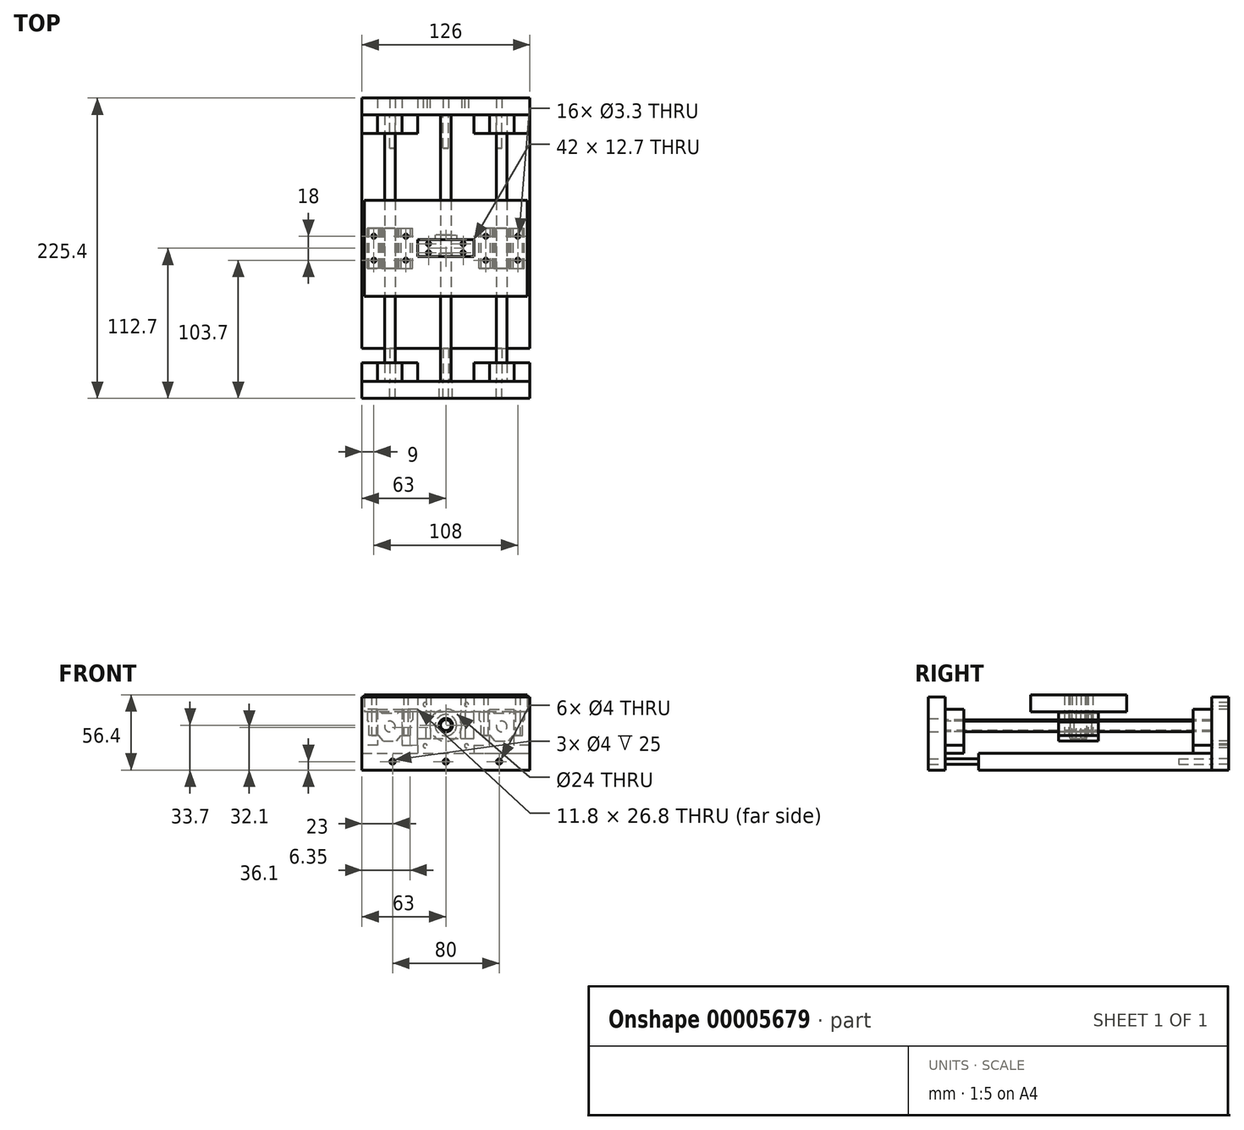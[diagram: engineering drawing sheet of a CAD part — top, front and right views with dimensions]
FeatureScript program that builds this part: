
annotation { "Feature Type Name" : "Feature", "Feature Type Description" : "" }
export const myFeature = defineFeature(function(context is Context, id is Id, definition is map)
    precondition{}
    {
        {
            var Q0;
            Q0=qCreatedBy(makeId("Top.planeOp"),FACE);
            var sketch = newSketch(context, id + "F0", { "sketchPlane" : qUnion([Q0])});
            skLineSegment(sketch, "E0.bottom", {"start": v(-63, 100) * mm, "end": v(63, 100) * mm});
            skLineSegment(sketch, "E0.top", {"start": v(-63, -100) * mm, "end": v(63, -100) * mm});
            skLineSegment(sketch, "E0.left", {"start": v(-63, 100) * mm, "end": v(-63, -100) * mm});
            skLineSegment(sketch, "E0.right", {"start": v(63, 100) * mm, "end": v(63, -100) * mm});
            skLineSegment(sketch, "E1", {"start": v(-63, 0) * mm, "end": v(63, 0) * mm, "construction": true});
            skSolve(sketch);
        }
        {
            var Q0;
            Q0=makeQuery(id+"F0.imprint","IMPRINT",FACE,{"disambiguationData":[TD([[makeQuery(id+"F0.imprint","IMPRINT",EDGE,{"derivedFrom":sQuery(id+"F0.wireOp",EDGE,"E0.bottom")}),-1.0]])]});
            extrude(context, id + "F1", {"entities" : qUnion([Q0]), "depth" : 12.7 * mm});
        }
        {
            var Q0;
            Q0=makeQuery(id+"F1.opExtrude","SWEPT_FACE",FACE,{"disambiguationData":[OSD([sQuery(id+"F0.wireOp",EDGE,"E0.bottom")])]});
            var sketch = newSketch(context, id + "F2", { "sketchPlane" : qUnion([Q0])});
            skPoint(sketch, "E2", {"position": v(0, 33.7) * mm});
            skCircle(sketch, "E3", {"center": v(0, 33.7) * mm, "radius": 12 * mm});
            skLineSegment(sketch, "E4.bottom", {"start": v(-63, 12.7) * mm, "end": v(63, 12.7) * mm, "construction": true});
            skLineSegment(sketch, "E4.top", {"start": v(-63, 54.7) * mm, "end": v(63, 54.7) * mm});
            skLineSegment(sketch, "E4.left", {"start": v(-63, 12.7) * mm, "end": v(-63, 54.7) * mm});
            skLineSegment(sketch, "E4.right", {"start": v(63, 12.7) * mm, "end": v(63, 54.7) * mm});
            skLineSegment(sketch, "E5", {"start": v(0, 54.7) * mm, "end": v(0, 12.7) * mm, "construction": true});
            skLineSegment(sketch, "E6", {"start": v(-63, 33.7) * mm, "end": v(63, 33.7) * mm, "construction": true});
            skLineSegment(sketch, "E7.rect.bottom", {"start": v(15.5, 49.2) * mm, "end": v(-15.5, 49.2) * mm, "construction": true});
            skLineSegment(sketch, "E7.rect.top", {"start": v(15.5, 18.2) * mm, "end": v(-15.5, 18.2) * mm, "construction": true});
            skLineSegment(sketch, "E7.rect.left", {"start": v(15.5, 49.2) * mm, "end": v(15.5, 18.2) * mm, "construction": true});
            skLineSegment(sketch, "E7.rect.right", {"start": v(-15.5, 49.2) * mm, "end": v(-15.5, 18.2) * mm, "construction": true});
            skCircle(sketch, "E8", {"center": v(-15.5, 49.2) * mm, "radius": 1.5 * mm});
            skCircle(sketch, "E9", {"center": v(15.5, 49.2) * mm, "radius": 1.5 * mm});
            skCircle(sketch, "E10", {"center": v(-15.5, 18.2) * mm, "radius": 1.5 * mm});
            skCircle(sketch, "E11", {"center": v(15.5, 18.2) * mm, "radius": 1.5 * mm});
            skLineSegment(sketch, "E12.rect.bottom", {"start": v(21, 12.7) * mm, "end": v(-21, 12.7) * mm, "construction": true});
            skLineSegment(sketch, "E12.rect.top", {"start": v(21, 54.7) * mm, "end": v(-21, 54.7) * mm, "construction": true});
            skLineSegment(sketch, "E12.rect.left", {"start": v(21, 12.7) * mm, "end": v(21, 54.7) * mm, "construction": true});
            skLineSegment(sketch, "E12.rect.right", {"start": v(-21, 12.7) * mm, "end": v(-21, 54.7) * mm, "construction": true});
            skLineSegment(sketch, "E13.0", {"start": v(-63, 12.7) * mm, "end": v(-63, 0) * mm});
            skLineSegment(sketch, "E14.0", {"start": v(63, 12.7) * mm, "end": v(63, 0) * mm});
            skLineSegment(sketch, "E15.0", {"start": v(63, 0) * mm, "end": v(-63, 0) * mm});
            skLineSegment(sketch, "E16.0.0", {"start": v(-63, 0) * mm, "end": v(63, 0) * mm});
            skLineSegment(sketch, "E16.0.1", {"start": v(63, 0) * mm, "end": v(63, 12.7) * mm});
            skLineSegment(sketch, "E16.0.2", {"start": v(63, 12.7) * mm, "end": v(-63, 12.7) * mm});
            skLineSegment(sketch, "E17", {"start": v(-63, 6.35) * mm, "end": v(63, 6.35) * mm, "construction": true});
            skLineSegment(sketch, "E18", {"start": v(0, 0) * mm, "end": v(0, 12.7) * mm, "construction": true});
            skPoint(sketch, "E19", {"position": v(0, 6.35) * mm});
            skCircle(sketch, "E20", {"center": v(0, 6.35) * mm, "radius": 2 * mm});
            skCircle(sketch, "E21.1.0.0", {"center": v(40, 6.35) * mm, "radius": 2 * mm});
            skLineSegment(sketch, "E21.direction1", {"start": v(0, 6.35) * mm, "end": v(40, 6.35) * mm, "construction": true});
            skCircle(sketch, "E22.1.0.0", {"center": v(-40, 6.35) * mm, "radius": 2 * mm});
            skLineSegment(sketch, "E22.direction1", {"start": v(0, 6.35) * mm, "end": v(-40, 6.35) * mm, "construction": true});
            skSolve(sketch);
        }
        {
            var Q0;
            Q0=makeQuery(id+"F2.imprint","IMPRINT",FACE,{"disambiguationData":[TD([[makeQuery(id+"F2.imprint","IMPRINT",EDGE,{"derivedFrom":sQuery(id+"F2.wireOp",EDGE,"E22.1.0.0")}),1.0]])]});
            var Q1;
            Q1=makeQuery(id+"F2.imprint","IMPRINT",FACE,{"disambiguationData":[TD([[makeQuery(id+"F2.imprint","IMPRINT",EDGE,{"derivedFrom":sQuery(id+"F2.wireOp",EDGE,"E20")}),1.0]])]});
            var Q2;
            Q2=makeQuery(id+"F2.imprint","IMPRINT",FACE,{"disambiguationData":[TD([[makeQuery(id+"F2.imprint","IMPRINT",EDGE,{"derivedFrom":sQuery(id+"F2.wireOp",EDGE,"E21.1.0.0")}),1.0]])]});
            extrude(context, id + "F3", {"entities" : qUnion([Q0, Q1, Q2]), "operationType" : NewBodyOperationType.REMOVE, "oppositeDirection" : true, "depth" : 25 * mm});
        }
        {
            var Q0;
            Q0 = qSketchRegion(id + "F2", true);
            extrude(context, id + "F4", {"entities" : qUnion([Q0]), "depth" : 12.7 * mm});
        }
        {
            var Q0;
            Q0=makeQuery(id+"F1.opExtrude","SWEPT_FACE",FACE,{"disambiguationData":[OSD([sQuery(id+"F0.wireOp",EDGE,"E0.top")])]});
            var sketch = newSketch(context, id + "F5", { "sketchPlane" : qUnion([Q0])});
            skLineSegment(sketch, "E23.0", {"start": v(63, 54.7) * mm, "end": v(-63, 54.7) * mm});
            skLineSegment(sketch, "E24.0", {"start": v(-63, 12.7) * mm, "end": v(63, 12.7) * mm, "construction": true});
            skLineSegment(sketch, "E25.0", {"start": v(-63, 0) * mm, "end": v(63, 0) * mm});
            skLineSegment(sketch, "E26.0", {"start": v(-63, 54.7) * mm, "end": v(-63, 0) * mm});
            skLineSegment(sketch, "E27.0", {"start": v(63, 54.7) * mm, "end": v(63, 0) * mm});
            skCircle(sketch, "E28.0", {"center": v(40, 6.35) * mm, "radius": 2 * mm});
            skCircle(sketch, "E29.0", {"center": v(0, 6.35) * mm, "radius": 2 * mm});
            skCircle(sketch, "E30.0", {"center": v(-40, 6.35) * mm, "radius": 2 * mm});
            skLineSegment(sketch, "E31", {"start": v(0, 54.7) * mm, "end": v(0, 12.7) * mm, "construction": true});
            skPoint(sketch, "E32", {"position": v(0, 33.7) * mm});
            skCircle(sketch, "E33", {"center": v(0, 33.7) * mm, "radius": 4 * mm});
            skSolve(sketch);
        }
        {
            var Q0;
            {var subQ2=sQuery(id+"F5.wireOp",EDGE,"E25.0");Q0=makeQuery(id+"F5.imprint","IMPRINT",FACE,{"disambiguationData":[TD([[makeQuery(id+"F5.imprint","IMPRINT",EDGE,{"derivedFrom":subQ2}),1.0]])]});}
            var Q1;
            {var subQ2=sQuery(id+"F5.wireOp",EDGE,"E23.0");Q1=makeQuery(id+"F5.imprint","IMPRINT",FACE,{"disambiguationData":[TD([[makeQuery(id+"F5.imprint","IMPRINT",EDGE,{"derivedFrom":subQ2}),1.0]])]});}
            extrude(context, id + "F6", {"entities" : qUnion([Q0, Q1]), "depth" : 12.7 * mm});
        }
        {
            var Q0;
            Q0=makeQuery(id+"F1.opExtrude","SWEPT_FACE",FACE,{"disambiguationData":[OSD([sQuery(id+"F0.wireOp",EDGE,"E0.top")])]});
            var sketch = newSketch(context, id + "F7", { "sketchPlane" : qUnion([Q0])});
            skCircle(sketch, "E34.0", {"center": v(-40, 6.35) * mm, "radius": 2 * mm});
            skCircle(sketch, "E35.0", {"center": v(0, 6.35) * mm, "radius": 2 * mm});
            skCircle(sketch, "E36.0", {"center": v(40, 6.35) * mm, "radius": 2 * mm});
            skSolve(sketch);
        }
        {
            var Q0;
            Q0=makeQuery(id+"F7.imprint","IMPRINT",FACE,{"disambiguationData":[TD([[makeQuery(id+"F7.imprint","IMPRINT",EDGE,{"derivedFrom":sQuery(id+"F7.wireOp",EDGE,"E34.0")}),-1.0]])]});
            var Q1;
            Q1=makeQuery(id+"F7.imprint","IMPRINT",FACE,{"disambiguationData":[TD([[makeQuery(id+"F7.imprint","IMPRINT",EDGE,{"derivedFrom":sQuery(id+"F7.wireOp",EDGE,"E35.0")}),-1.0]])]});
            var Q2;
            Q2=makeQuery(id+"F7.imprint","IMPRINT",FACE,{"disambiguationData":[TD([[makeQuery(id+"F7.imprint","IMPRINT",EDGE,{"derivedFrom":sQuery(id+"F7.wireOp",EDGE,"E36.0")}),-1.0]])]});
            extrude(context, id + "F8", {"entities" : qUnion([Q0, Q1, Q2]), "operationType" : NewBodyOperationType.REMOVE, "oppositeDirection" : true, "depth" : 25 * mm});
        }
        {
            var Q0;
            Q0=makeQuery(id+"F1.opExtrude","CAP_FACE",FACE,{"disambiguationData":[OSD([sQuery(id+"F0.wireOp",EDGE,"E0.bottom"),sQuery(id+"F0.wireOp",EDGE,"E0.top"),sQuery(id+"F0.wireOp",EDGE,"E0.left"),sQuery(id+"F0.wireOp",EDGE,"E0.right")])],"isStart":false});
            var sketch = newSketch(context, id + "F9", { "sketchPlane" : qUnion([Q0])});
            skLineSegment(sketch, "E37.bottom", {"start": v(-63, 100) * mm, "end": v(-21, 100) * mm});
            skLineSegment(sketch, "E37.top", {"start": v(-63, 86) * mm, "end": v(-21, 86) * mm});
            skLineSegment(sketch, "E37.left", {"start": v(-63, 100) * mm, "end": v(-63, 86) * mm});
            skLineSegment(sketch, "E37.right", {"start": v(-21, 100) * mm, "end": v(-21, 86) * mm});
            skSolve(sketch);
        }
        {
            var Q0;
            Q0=makeQuery(id+"F9.imprint","IMPRINT",FACE,{"disambiguationData":[TD([[makeQuery(id+"F9.imprint","IMPRINT",EDGE,{"derivedFrom":sQuery(id+"F9.wireOp",EDGE,"E37.bottom")}),-1.0]])]});
            extrude(context, id + "F10", {"entities" : qUnion([Q0]), "depth" : 32.8 * mm});
        }
        {
            var Q0;
            Q0=makeQuery(id+"F10.opExtrude","SWEPT_FACE",FACE,{"disambiguationData":[OSD([sQuery(id+"F9.wireOp",EDGE,"E37.top")])]});
            var sketch = newSketch(context, id + "F11", { "sketchPlane" : qUnion([Q0])});
            skLineSegment(sketch, "E38", {"start": v(-21, 18.7) * mm, "end": v(-32.8, 18.7) * mm});
            skLineSegment(sketch, "E39", {"start": v(-32.8, 18.7) * mm, "end": v(-32.8, 45.5) * mm});
            skLineSegment(sketch, "E40", {"start": v(-42, 45.5) * mm, "end": v(-42, 12.7) * mm, "construction": true});
            skLineSegment(sketch, "E41.0.MirrorCS", {"start": v(-51.2, 18.7) * mm, "end": v(-51.2, 45.5) * mm});
            skLineSegment(sketch, "E42.0.MirrorCS", {"start": v(-63, 18.7) * mm, "end": v(-51.2, 18.7) * mm});
            skSolve(sketch);
        }
        {
            var Q0;
            {var subQ5=sQuery(id+"F11.wireOp",EDGE,"E38");Q0=makeQuery(id+"F11.imprint","IMPRINT",FACE,{"disambiguationData":[TD([[makeQuery(id+"F11.imprint","IMPRINT",EDGE,{"derivedFrom":subQ5}),-1.0]])]});}
            var Q1;
            {var subQ2=sQuery(id+"F11.wireOp",EDGE,"E41.0.MirrorCS");Q1=makeQuery(id+"F11.imprint","IMPRINT",FACE,{"disambiguationData":[TD([[makeQuery(id+"F11.imprint","IMPRINT",EDGE,{"derivedFrom":subQ2}),1.0]])]});}
            extrude(context, id + "F12", {"entities" : qUnion([Q0, Q1]), "operationType" : NewBodyOperationType.REMOVE, "endBound" : BoundingType.THROUGH_ALL, "oppositeDirection" : true, "depth" : 25 * mm});
        }
        {
            var Q0;
            Q0=makeQuery(id+"F10.opExtrude","SWEPT_BODY",BODY,{"disambiguationData":[OSD([sQuery(id+"F9.wireOp",EDGE,"E37.bottom"),sQuery(id+"F9.wireOp",EDGE,"E37.top"),sQuery(id+"F9.wireOp",EDGE,"E37.left"),sQuery(id+"F9.wireOp",EDGE,"E37.right")])]});
            transform(context, id + "F13", {"entities" : qUnion([Q0]), "transformType" : TransformType.TRANSLATION_3D, "dx" : 0 * mm, "dy" : -186 * mm, "dz" : 0 * mm, "makeCopy" : true});
        }
        {
            var Q0;
            Q0=makeQuery(id+"F10.opExtrude","SWEPT_BODY",BODY,{"disambiguationData":[OSD([sQuery(id+"F9.wireOp",EDGE,"E37.bottom"),sQuery(id+"F9.wireOp",EDGE,"E37.top"),sQuery(id+"F9.wireOp",EDGE,"E37.left"),sQuery(id+"F9.wireOp",EDGE,"E37.right")])]});
            var Q1;
            Q1=makeQuery(id+"F13.opPattern","COPY",BODY,{"derivedFrom":makeQuery(id+"F10.opExtrude","SWEPT_BODY",BODY,{"disambiguationData":[OSD([sQuery(id+"F9.wireOp",EDGE,"E37.bottom"),sQuery(id+"F9.wireOp",EDGE,"E37.top"),sQuery(id+"F9.wireOp",EDGE,"E37.left"),sQuery(id+"F9.wireOp",EDGE,"E37.right")])]}),"instanceName":"1"});
            transform(context, id + "F14", {"entities" : qUnion([Q0, Q1]), "transformType" : TransformType.TRANSLATION_3D, "dx" : 84 * mm, "dy" : 0 * mm, "dz" : 0 * mm, "makeCopy" : true});
        }
        {
            var Q0;
            Q0=makeQuery(id+"F13.opPattern","COPY",FACE,{"derivedFrom":makeQuery(id+"F10.opExtrude","SWEPT_FACE",FACE,{"disambiguationData":[OSD([sQuery(id+"F9.wireOp",EDGE,"E37.top")])]}),"instanceName":"1"});
            var sketch = newSketch(context, id + "F15", { "sketchPlane" : qUnion([Q0])});
            skLineSegment(sketch, "E43", {"start": v(-42, 45.5) * mm, "end": v(-42, 12.7) * mm, "construction": true});
            skCircle(sketch, "E44", {"center": v(-42, 32.7) * mm, "radius": 4 * mm});
            skSolve(sketch);
        }
        {
            var Q0;
            Q0=makeQuery(id+"F15.imprint","IMPRINT",FACE,{"disambiguationData":[TD([[makeQuery(id+"F15.imprint","IMPRINT",EDGE,{"derivedFrom":sQuery(id+"F15.wireOp",EDGE,"E44")}),1.0]])]});
            var Q1;
            Q1=sQuery(id+"F15.wireOp",EDGE,"E44");
            extrude(context, id + "F16", {"entities" : qUnion([Q0]), "surfaceEntities" : qUnion([Q1]), "oppositeDirection" : true, "depth" : 200 * mm});
        }
        {
            var Q0;
            Q0=makeQuery(id+"F13.opPattern","COPY",BODY,{"derivedFrom":makeQuery(id+"F10.opExtrude","SWEPT_BODY",BODY,{"disambiguationData":[OSD([sQuery(id+"F9.wireOp",EDGE,"E37.bottom"),sQuery(id+"F9.wireOp",EDGE,"E37.top"),sQuery(id+"F9.wireOp",EDGE,"E37.left"),sQuery(id+"F9.wireOp",EDGE,"E37.right")])]}),"instanceName":"1"});
            transform(context, id + "F17", {"entities" : qUnion([Q0]), "transformType" : TransformType.TRANSLATION_3D, "dx" : 84 * mm, "dy" : 0 * mm, "dz" : 0 * mm, "makeCopy" : true});
        }
        {
            var Q0;
            Q0=makeQuery(id+"F17.opPattern","COPY",BODY,{"derivedFrom":makeQuery(id+"F13.opPattern","COPY",BODY,{"derivedFrom":makeQuery(id+"F10.opExtrude","SWEPT_BODY",BODY,{"disambiguationData":[OSD([sQuery(id+"F9.wireOp",EDGE,"E37.bottom"),sQuery(id+"F9.wireOp",EDGE,"E37.top"),sQuery(id+"F9.wireOp",EDGE,"E37.left"),sQuery(id+"F9.wireOp",EDGE,"E37.right")])]}),"instanceName":"1"}),"instanceName":"1"});
            deleteBodies(context, id + "F18", {"entities" : qUnion([Q0])});
        }
        {
            var Q0;
            Q0=makeQuery(id+"F16.opExtrude","SWEPT_BODY",BODY,{"disambiguationData":[OSD([sQuery(id+"F15.wireOp",EDGE,"E44")])]});
            transform(context, id + "F19", {"entities" : qUnion([Q0]), "transformType" : TransformType.TRANSLATION_3D, "dx" : 84 * mm, "dy" : 0 * mm, "dz" : 0 * mm, "makeCopy" : true});
        }
        {
            var Q0;
            Q0=qCreatedBy(makeId("Front.planeOp"),FACE);
            var sketch = newSketch(context, id + "F20", { "sketchPlane" : qUnion([Q0])});
            skLineSegment(sketch, "E45.rect.bottom", {"start": v(-25, 21.7) * mm, "end": v(-35, 21.7) * mm});
            skLineSegment(sketch, "E45.rect.top", {"start": v(-37, 43.7) * mm, "end": v(-47, 43.7) * mm});
            skLineSegment(sketch, "E45.rect.left", {"start": v(-25, 21.7) * mm, "end": v(-25, 27.7) * mm});
            skLineSegment(sketch, "E45.rect.right", {"start": v(-59, 21.7) * mm, "end": v(-59, 27.7) * mm});
            skPoint(sketch, "E45.rect.middle", {"position": v(-42, 32.7) * mm});
            skCircle(sketch, "E46", {"center": v(-42, 32.7) * mm, "radius": 4 * mm});
            skLineSegment(sketch, "E47", {"start": v(-42, 43.7) * mm, "end": v(-42, 21.7) * mm, "construction": true});
            skLineSegment(sketch, "E48", {"start": v(-37, 43.7) * mm, "end": v(-33.5, 39.4) * mm});
            skLineSegment(sketch, "E49", {"start": v(-33.5, 39.4) * mm, "end": v(-26.5, 39.4) * mm});
            skCircle(sketch, "E50", {"center": v(-42, 32.7) * mm, "radius": 7.5 * mm});
            skLineSegment(sketch, "E51.0.MirrorCS", {"start": v(-47, 43.7) * mm, "end": v(-50.5, 39.4) * mm});
            skLineSegment(sketch, "E52.0.MirrorCS", {"start": v(-50.5, 39.4) * mm, "end": v(-57.5, 39.4) * mm});
            skLineSegment(sketch, "E53", {"start": v(-42, 22.7) * mm, "end": v(-36, 22.7) * mm});
            skLineSegment(sketch, "E54", {"start": v(-36, 22.7) * mm, "end": v(-35, 21.7) * mm});
            skLineSegment(sketch, "E55.0.MirrorCS", {"start": v(-42, 22.7) * mm, "end": v(-48, 22.7) * mm});
            skLineSegment(sketch, "E56.0.MirrorCS", {"start": v(-48, 22.7) * mm, "end": v(-49, 21.7) * mm});
            skLineSegment(sketch, "E57.trimOffspring", {"start": v(-49, 21.7) * mm, "end": v(-59, 21.7) * mm});
            skLineSegment(sketch, "E58", {"start": v(-26.5, 39.4) * mm, "end": v(-26.5, 29.4) * mm});
            skLineSegment(sketch, "E59", {"start": v(-26.5, 29.4) * mm, "end": v(-25, 27.7) * mm});
            skLineSegment(sketch, "E60.0.MirrorCS", {"start": v(-57.5, 39.4) * mm, "end": v(-57.5, 29.4) * mm});
            skLineSegment(sketch, "E61.0.MirrorCS", {"start": v(-57.5, 29.4) * mm, "end": v(-59, 27.7) * mm});
            skSolve(sketch);
        }
        {
            var Q0;
            Q0=makeQuery(id+"F20.imprint","IMPRINT",FACE,{"disambiguationData":[TD([[makeQuery(id+"F20.imprint","IMPRINT",EDGE,{"derivedFrom":sQuery(id+"F20.wireOp",EDGE,"E45.rect.bottom")}),-1.0]])]});
            var Q1;
            Q1=makeQuery(id+"F20.imprint","IMPRINT",FACE,{"disambiguationData":[TD([[makeQuery(id+"F20.imprint","IMPRINT",EDGE,{"derivedFrom":sQuery(id+"F20.wireOp",EDGE,"E46")}),-1.0]])]});
            extrude(context, id + "F21", {"entities" : qUnion([Q0, Q1]), "depth" : 30 * mm, "symmetric" : true});
        }
        {
            var Q0;
            Q0=makeQuery(id+"F21.opExtrude","SWEPT_BODY",BODY,{"disambiguationData":[OSD([sQuery(id+"F20.wireOp",EDGE,"E45.rect.bottom"),sQuery(id+"F20.wireOp",EDGE,"E45.rect.top"),sQuery(id+"F20.wireOp",EDGE,"E45.rect.left"),sQuery(id+"F20.wireOp",EDGE,"E45.rect.right"),sQuery(id+"F20.wireOp",EDGE,"E46"),sQuery(id+"F20.wireOp",EDGE,"E48"),sQuery(id+"F20.wireOp",EDGE,"E49"),sQuery(id+"F20.wireOp",EDGE,"E51.0.MirrorCS"),sQuery(id+"F20.wireOp",EDGE,"E52.0.MirrorCS"),sQuery(id+"F20.wireOp",EDGE,"E53"),sQuery(id+"F20.wireOp",EDGE,"E54"),sQuery(id+"F20.wireOp",EDGE,"E55.0.MirrorCS"),sQuery(id+"F20.wireOp",EDGE,"E56.0.MirrorCS"),sQuery(id+"F20.wireOp",EDGE,"E57.trimOffspring"),sQuery(id+"F20.wireOp",EDGE,"E58"),sQuery(id+"F20.wireOp",EDGE,"E59"),sQuery(id+"F20.wireOp",EDGE,"E60.0.MirrorCS"),sQuery(id+"F20.wireOp",EDGE,"E61.0.MirrorCS")])]});
            var Q1;
            Q1=makeQuery(id+"F21.opExtrude","SWEPT_FACE",FACE,{"disambiguationData":[OSD([sQuery(id+"F20.wireOp",EDGE,"E46")])]});
            transform(context, id + "F22", {"entities" : qUnion([Q0]), "transformType" : TransformType.ROTATION, "transformAxis" : qUnion([Q1]), "angle" : 180 * degree, "makeCopy" : false});
        }
        {
            var Q0;
            Q0=makeQuery(id+"F21.opExtrude","SWEPT_FACE",FACE,{"disambiguationData":[OSD([sQuery(id+"F20.wireOp",EDGE,"E45.rect.top")])]});
            var sketch = newSketch(context, id + "F23", { "sketchPlane" : qUnion([Q0])});
            skCircle(sketch, "E62", {"center": v(-30, 9) * mm, "radius": 1.65 * mm});
            skLineSegment(sketch, "E63", {"start": v(-42, 15) * mm, "end": v(-42, -15) * mm, "construction": true});
            skCircle(sketch, "E64.0.MirrorC", {"center": v(-54, 9) * mm, "radius": 1.65 * mm});
            skLineSegment(sketch, "E65", {"start": v(-59, 0) * mm, "end": v(-25, 0) * mm, "construction": true});
            skCircle(sketch, "E66.0.MirrorC", {"center": v(-30, -9) * mm, "radius": 1.65 * mm});
            skCircle(sketch, "E67.0.MirrorC", {"center": v(-54, -9) * mm, "radius": 1.65 * mm});
            skSolve(sketch);
        }
        {
            var Q0;
            Q0=makeQuery(id+"F23.imprint","IMPRINT",FACE,{"disambiguationData":[TD([[makeQuery(id+"F23.imprint","IMPRINT",EDGE,{"derivedFrom":sQuery(id+"F23.wireOp",EDGE,"E66.0.MirrorC")}),-1.0]])]});
            var Q1;
            Q1=makeQuery(id+"F23.imprint","IMPRINT",FACE,{"disambiguationData":[TD([[makeQuery(id+"F23.imprint","IMPRINT",EDGE,{"derivedFrom":sQuery(id+"F23.wireOp",EDGE,"E62")}),1.0]])]});
            var Q2;
            Q2=makeQuery(id+"F23.imprint","IMPRINT",FACE,{"disambiguationData":[TD([[makeQuery(id+"F23.imprint","IMPRINT",EDGE,{"derivedFrom":sQuery(id+"F23.wireOp",EDGE,"E64.0.MirrorC")}),-1.0]])]});
            var Q3;
            Q3=makeQuery(id+"F23.imprint","IMPRINT",FACE,{"disambiguationData":[TD([[makeQuery(id+"F23.imprint","IMPRINT",EDGE,{"derivedFrom":sQuery(id+"F23.wireOp",EDGE,"E67.0.MirrorC")}),1.0]])]});
            extrude(context, id + "F24", {"entities" : qUnion([Q0, Q1, Q2, Q3]), "operationType" : NewBodyOperationType.REMOVE, "endBound" : BoundingType.THROUGH_ALL, "oppositeDirection" : true, "depth" : 25 * mm});
        }
        {
            var Q0;
            Q0=makeQuery(id+"F21.opExtrude","SWEPT_BODY",BODY,{"disambiguationData":[OSD([sQuery(id+"F20.wireOp",EDGE,"E45.rect.bottom"),sQuery(id+"F20.wireOp",EDGE,"E45.rect.top"),sQuery(id+"F20.wireOp",EDGE,"E45.rect.left"),sQuery(id+"F20.wireOp",EDGE,"E45.rect.right"),sQuery(id+"F20.wireOp",EDGE,"E46"),sQuery(id+"F20.wireOp",EDGE,"E48"),sQuery(id+"F20.wireOp",EDGE,"E49"),sQuery(id+"F20.wireOp",EDGE,"E51.0.MirrorCS"),sQuery(id+"F20.wireOp",EDGE,"E52.0.MirrorCS"),sQuery(id+"F20.wireOp",EDGE,"E53"),sQuery(id+"F20.wireOp",EDGE,"E54"),sQuery(id+"F20.wireOp",EDGE,"E55.0.MirrorCS"),sQuery(id+"F20.wireOp",EDGE,"E56.0.MirrorCS"),sQuery(id+"F20.wireOp",EDGE,"E57.trimOffspring"),sQuery(id+"F20.wireOp",EDGE,"E58"),sQuery(id+"F20.wireOp",EDGE,"E59"),sQuery(id+"F20.wireOp",EDGE,"E60.0.MirrorCS"),sQuery(id+"F20.wireOp",EDGE,"E61.0.MirrorCS")])]});
            transform(context, id + "F25", {"entities" : qUnion([Q0]), "transformType" : TransformType.TRANSLATION_3D, "dx" : 84 * mm, "dy" : 0 * mm, "dz" : 0 * mm, "makeCopy" : true});
        }
        {
            var Q0;
            Q0=makeQuery(id+"F21.opExtrude","SWEPT_FACE",FACE,{"disambiguationData":[OSD([sQuery(id+"F20.wireOp",EDGE,"E45.rect.bottom")])]});
            var sketch = newSketch(context, id + "F26", { "sketchPlane" : qUnion([Q0])});
            skLineSegment(sketch, "E68.0", {"start": v(-63, 100) * mm, "end": v(-63, -100) * mm});
            skLineSegment(sketch, "E69.0", {"start": v(63, 100) * mm, "end": v(63, -100) * mm});
            skCircle(sketch, "E70.0", {"center": v(-54, 9) * mm, "radius": 1.65 * mm});
            skCircle(sketch, "E71.0", {"center": v(-54, -9) * mm, "radius": 1.65 * mm});
            skCircle(sketch, "E72.0", {"center": v(-30, -9) * mm, "radius": 1.65 * mm});
            skCircle(sketch, "E73.0", {"center": v(-30, 9) * mm, "radius": 1.65 * mm});
            skCircle(sketch, "E74.0", {"center": v(30, 9) * mm, "radius": 1.65 * mm});
            skCircle(sketch, "E75.0", {"center": v(30, -9) * mm, "radius": 1.65 * mm});
            skCircle(sketch, "E76.0", {"center": v(54, 9) * mm, "radius": 1.65 * mm});
            skCircle(sketch, "E77.0", {"center": v(54, -9) * mm, "radius": 1.65 * mm});
            skLineSegment(sketch, "E78", {"start": v(-63, 0) * mm, "end": v(63, 0) * mm, "construction": true});
            skLineSegment(sketch, "E79.rect.bottom", {"start": v(61, 36) * mm, "end": v(-61, 36) * mm});
            skLineSegment(sketch, "E79.rect.top", {"start": v(61, -36) * mm, "end": v(-61, -36) * mm});
            skLineSegment(sketch, "E79.rect.left", {"start": v(61, 36) * mm, "end": v(61, -36) * mm});
            skLineSegment(sketch, "E79.rect.right", {"start": v(-61, 36) * mm, "end": v(-61, -36) * mm});
            skPoint(sketch, "E79.rect.middle", {"position": v(0, 0) * mm});
            skSolve(sketch);
        }
        {
            var Q0;
            Q0 = qSketchRegion(id + "F26", true);
            extrude(context, id + "F27", {"entities" : qUnion([Q0]), "depth" : 12.7 * mm});
        }
        {
            var Q0;
            Q0=makeQuery(id+"F27.opExtrude","CAP_FACE",FACE,{"disambiguationData":[OSD([sQuery(id+"F26.wireOp",EDGE,"E70.0"),sQuery(id+"F26.wireOp",EDGE,"E71.0"),sQuery(id+"F26.wireOp",EDGE,"E72.0"),sQuery(id+"F26.wireOp",EDGE,"E73.0"),sQuery(id+"F26.wireOp",EDGE,"E74.0"),sQuery(id+"F26.wireOp",EDGE,"E75.0"),sQuery(id+"F26.wireOp",EDGE,"E76.0"),sQuery(id+"F26.wireOp",EDGE,"E77.0"),sQuery(id+"F26.wireOp",EDGE,"E79.rect.bottom"),sQuery(id+"F26.wireOp",EDGE,"E79.rect.top"),sQuery(id+"F26.wireOp",EDGE,"E79.rect.left"),sQuery(id+"F26.wireOp",EDGE,"E79.rect.right")])],"isStart":true});
            var sketch = newSketch(context, id + "F28", { "sketchPlane" : qUnion([Q0])});
            skLineSegment(sketch, "E80", {"start": v(0, -36) * mm, "end": v(0, 36) * mm, "construction": true});
            skLineSegment(sketch, "E81.rect.bottom", {"start": v(-21, 6.35) * mm, "end": v(21, 6.35) * mm});
            skLineSegment(sketch, "E81.rect.top", {"start": v(-21, -6.35) * mm, "end": v(21, -6.35) * mm});
            skLineSegment(sketch, "E81.rect.left", {"start": v(-21, 6.35) * mm, "end": v(-21, -6.35) * mm});
            skLineSegment(sketch, "E81.rect.right", {"start": v(21, 6.35) * mm, "end": v(21, -6.35) * mm});
            skPoint(sketch, "E81.rect.middle", {"position": v(0, 0) * mm});
            skLineSegment(sketch, "E82", {"start": v(21, 0) * mm, "end": v(-21, 0) * mm, "construction": true});
            skCircle(sketch, "E83", {"center": v(13, -3.35) * mm, "radius": 1.65 * mm});
            skCircle(sketch, "E84.0.MirrorC", {"center": v(-13, -3.35) * mm, "radius": 1.65 * mm});
            skCircle(sketch, "E85.0.MirrorC", {"center": v(13, 3.35) * mm, "radius": 1.65 * mm});
            skCircle(sketch, "E86.0.MirrorC", {"center": v(-13, 3.35) * mm, "radius": 1.65 * mm});
            skSolve(sketch);
        }
        {
            var Q0;
            Q0=makeQuery(id+"F28.imprint","IMPRINT",FACE,{"disambiguationData":[TD([[makeQuery(id+"F28.imprint","IMPRINT",EDGE,{"derivedFrom":sQuery(id+"F28.wireOp",EDGE,"E81.rect.bottom")}),-1.0]])]});
            extrude(context, id + "F29", {"entities" : qUnion([Q0]), "depth" : 20 * mm});
        }
        {
            var Q0;
            Q0=makeQuery(id+"F29.opExtrude","SWEPT_FACE",FACE,{"disambiguationData":[OSD([sQuery(id+"F28.wireOp",EDGE,"E81.rect.top")])]});
            var sketch = newSketch(context, id + "F30", { "sketchPlane" : qUnion([Q0])});
            skPoint(sketch, "E87.0", {"position": v(0, 33.7) * mm});
            skCircle(sketch, "E88", {"center": v(0, 33.7) * mm, "radius": 5 * mm});
            skSolve(sketch);
        }
        {
            var Q0;
            Q0=makeQuery(id+"F30.imprint","IMPRINT",FACE,{"disambiguationData":[TD([[makeQuery(id+"F30.imprint","IMPRINT",EDGE,{"derivedFrom":sQuery(id+"F30.wireOp",EDGE,"E88")}),1.0]])]});
            extrude(context, id + "F31", {"entities" : qUnion([Q0]), "operationType" : NewBodyOperationType.REMOVE, "endBound" : BoundingType.THROUGH_ALL, "oppositeDirection" : true, "depth" : 25 * mm});
        }
        {
            var Q0;
            Q0=makeQuery(id+"F29.opExtrude","SWEPT_FACE",FACE,{"disambiguationData":[OSD([sQuery(id+"F28.wireOp",EDGE,"E81.rect.top")])]});
            var sketch = newSketch(context, id + "F32", { "sketchPlane" : qUnion([Q0])});
            skPoint(sketch, "E89.0", {"position": v(0, 33.7) * mm});
            skCircle(sketch, "E90", {"center": v(0, 33.7) * mm, "radius": 4 * mm});
            skCircle(sketch, "E91", {"center": v(0, 33.7) * mm, "radius": 8 * mm});
            skCircle(sketch, "E92", {"center": v(0, 33.7) * mm, "radius": 5 * mm});
            skSolve(sketch);
        }
        {
            var Q0;
            Q0 = qSketchRegion(id + "F32", true);
            var Q1;
            Q1=makeQuery(id+"F32.imprint","IMPRINT",FACE,{"disambiguationData":[TD([[makeQuery(id+"F32.imprint","IMPRINT",EDGE,{"derivedFrom":sQuery(id+"F32.wireOp",EDGE,"E90")}),-1.0]])]});
            extrude(context, id + "F33", {"entities" : qUnion([Q0, Q1]), "depth" : 3.5 * mm});
        }
        {
            var Q0;
            Q0=makeQuery(id+"F32.imprint","IMPRINT",FACE,{"disambiguationData":[TD([[makeQuery(id+"F32.imprint","IMPRINT",EDGE,{"derivedFrom":sQuery(id+"F32.wireOp",EDGE,"E90")}),-1.0]])]});
            extrude(context, id + "F34", {"entities" : qUnion([Q0]), "operationType" : NewBodyOperationType.ADD, "oppositeDirection" : true, "depth" : 10 * mm});
        }
        {
            var Q0;
            Q0=makeQuery(id+"F16.opExtrude","SWEPT_BODY",BODY,{"disambiguationData":[OSD([sQuery(id+"F15.wireOp",EDGE,"E44")])]});
            transform(context, id + "F35", {"entities" : qUnion([Q0]), "transformType" : TransformType.TRANSLATION_3D, "dx" : 42 * mm, "dy" : 0 * mm, "dz" : 1 * mm, "makeCopy" : true});
        }
        {
            var Q0;
            Q0=makeQuery(id+"F28.imprint","IMPRINT",FACE,{"disambiguationData":[TD([[makeQuery(id+"F28.imprint","IMPRINT",EDGE,{"derivedFrom":sQuery(id+"F28.wireOp",EDGE,"E86.0.MirrorC")}),1.0]])]});
            var Q1;
            Q1=makeQuery(id+"F28.imprint","IMPRINT",FACE,{"disambiguationData":[TD([[makeQuery(id+"F28.imprint","IMPRINT",EDGE,{"derivedFrom":sQuery(id+"F28.wireOp",EDGE,"E85.0.MirrorC")}),-1.0]])]});
            var Q2;
            Q2=makeQuery(id+"F28.imprint","IMPRINT",FACE,{"disambiguationData":[TD([[makeQuery(id+"F28.imprint","IMPRINT",EDGE,{"derivedFrom":sQuery(id+"F28.wireOp",EDGE,"E83")}),1.0]])]});
            var Q3;
            Q3=makeQuery(id+"F28.imprint","IMPRINT",FACE,{"disambiguationData":[TD([[makeQuery(id+"F28.imprint","IMPRINT",EDGE,{"derivedFrom":sQuery(id+"F28.wireOp",EDGE,"E84.0.MirrorC")}),-1.0]])]});
            extrude(context, id + "F36", {"entities" : qUnion([Q0, Q1, Q2, Q3]), "operationType" : NewBodyOperationType.REMOVE, "endBound" : BoundingType.THROUGH_ALL, "oppositeDirection" : true, "depth" : 25 * mm});
        }
    });
